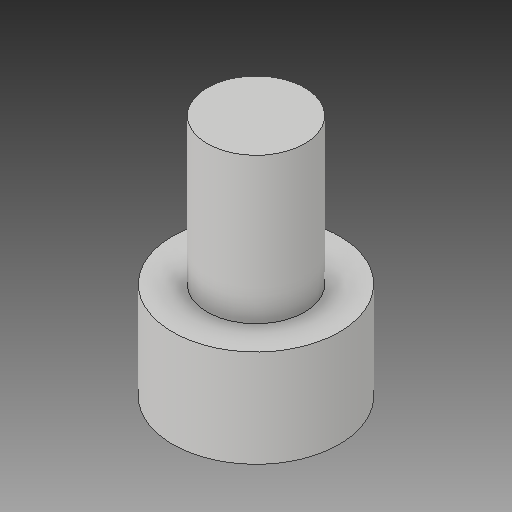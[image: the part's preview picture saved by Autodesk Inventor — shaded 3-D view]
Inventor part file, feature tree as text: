
AUTODESK INVENTOR PART (.ipt)
format: ipt  version: 2019 (Build 230136000, 136)  size: 97,792 bytes
history: native  units: mm
features: extrude x2, sketch x2
ambient origin geometry x8: Origin, YZ Plane, XZ Plane, XY Plane, X Axis, Y Axis, Z Axis, Center Point
bodies: Solid1 (feature_tree)
feature tree (4):
  extrude  "Extrusion1"  Depth=4.0mm TaperAngle=0.0deg
  extrude  "Extrusion2"  Depth=6.0mm TaperAngle=0.0deg
  sketch  "Sketch1"  dims[d0=6.85mm d1=4.0mm d2=0.0mm]
  sketch  "Sketch2"  dims[d3=4.0mm d4=6.0mm d5=0.0mm]
